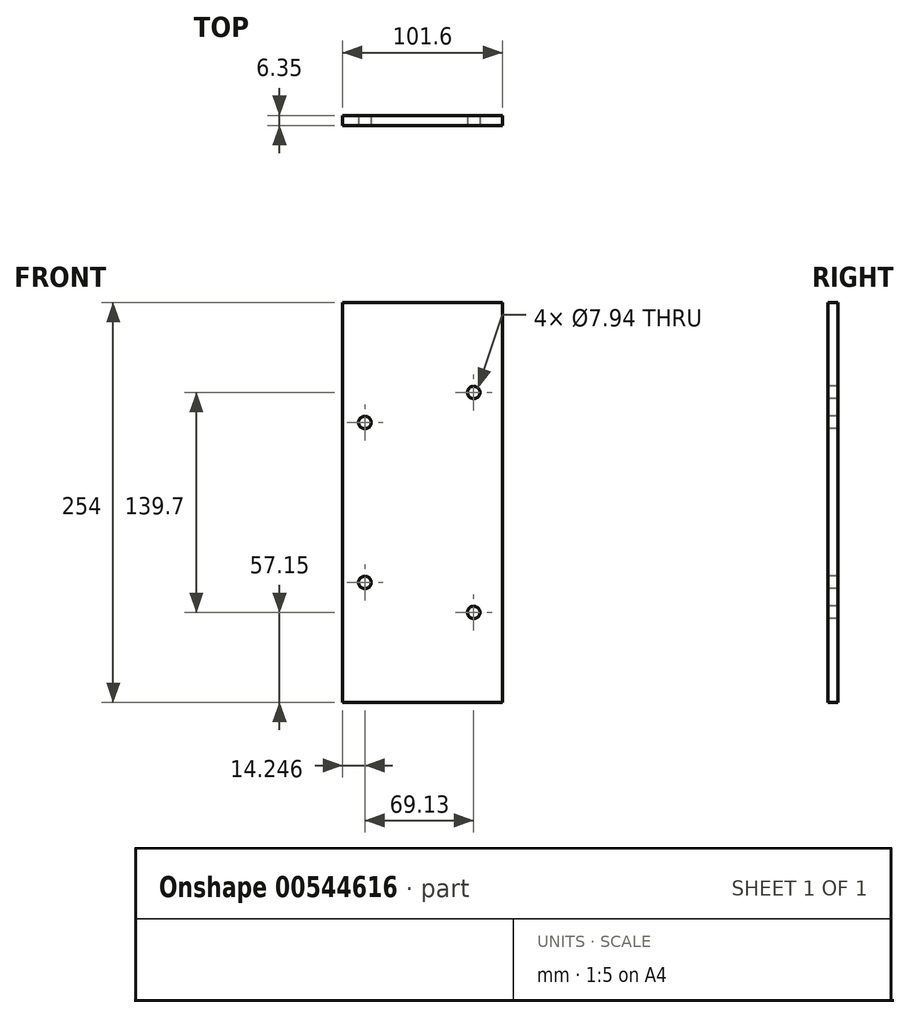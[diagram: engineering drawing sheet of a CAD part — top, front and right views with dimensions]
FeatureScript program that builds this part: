
annotation { "Feature Type Name" : "Feature", "Feature Type Description" : "" }
export const myFeature = defineFeature(function(context is Context, id is Id, definition is map)
    precondition{}
    {
        {
            var Q0;
            Q0=qCreatedBy(makeId("Front.planeOp"),FACE);
            var sketch = newSketch(context, id + "F0", { "sketchPlane" : qUnion([Q0])});
            skLineSegment(sketch, "E0.bottom", {"start": v(0, 0) * mm, "end": v(101.6, 0) * mm});
            skLineSegment(sketch, "E0.top", {"start": v(0, 254) * mm, "end": v(101.6, 254) * mm});
            skLineSegment(sketch, "E0.left", {"start": v(0, 0) * mm, "end": v(0, 254) * mm});
            skLineSegment(sketch, "E0.right", {"start": v(101.6, 0) * mm, "end": v(101.6, 254) * mm});
            skSolve(sketch);
        }
        {
            var Q0;
            Q0 = qSketchRegion(id + "F0", true);
            extrude(context, id + "F1", {"entities" : qUnion([Q0]), "depth" : 6.35 * mm, "offsetDistance" : 25.4 * mm});
        }
        {
            var Q0;
            Q0=makeQuery(id+"F1.opExtrude","CAP_FACE",FACE,{"disambiguationData":[OSD([sQuery(id+"F0.wireOp",EDGE,"E0.bottom"),sQuery(id+"F0.wireOp",EDGE,"E0.top"),sQuery(id+"F0.wireOp",EDGE,"E0.left"),sQuery(id+"F0.wireOp",EDGE,"E0.right")])],"isStart":false});
            var sketch = newSketch(context, id + "F2", { "sketchPlane" : qUnion([Q0])});
            skPoint(sketch, "E1", {"position": v(83.38, 57.15) * mm});
            skPoint(sketch, "E2", {"position": v(83.38, 196.85) * mm});
            skSolve(sketch);
        }
        {
            var Q0;
            Q0=sQuery(id+"F2.wireOp",VERTEX,"E1");
            var Q1;
            Q1=sQuery(id+"F2.wireOp",VERTEX,"E2");
            var Q2;
            Q2=makeQuery(id+"F1.opExtrude","SWEPT_BODY",BODY,{"disambiguationData":[OSD([sQuery(id+"F0.wireOp",EDGE,"E0.bottom"),sQuery(id+"F0.wireOp",EDGE,"E0.top"),sQuery(id+"F0.wireOp",EDGE,"E0.left"),sQuery(id+"F0.wireOp",EDGE,"E0.right")])]});
            hole(context, id + "F3", {"style" : HoleStyle.SIMPLE, "endStyle" : HoleEndStyle.THROUGH, "holeDiameter" : 7.94 * mm, "majorDiameter" : 6.35 * mm, "isTappedThrough" : true, "tappedDepth" : 12.7 * mm, "tapClearance" : 3, "locations" : qUnion([Q0, Q1]), "scope" : qUnion([Q2])});
        }
        {
            var Q0;
            Q0=makeQuery(id+"F1.opExtrude","CAP_FACE",FACE,{"disambiguationData":[OSD([sQuery(id+"F0.wireOp",EDGE,"E0.bottom"),sQuery(id+"F0.wireOp",EDGE,"E0.top"),sQuery(id+"F0.wireOp",EDGE,"E0.left"),sQuery(id+"F0.wireOp",EDGE,"E0.right")])],"isStart":false});
            var sketch = newSketch(context, id + "F4", { "sketchPlane" : qUnion([Q0])});
            skPoint(sketch, "E3", {"position": v(14.25, 76.2) * mm});
            skPoint(sketch, "E4", {"position": v(14.25, 177.8) * mm});
            skSolve(sketch);
        }
        {
            var Q0;
            Q0=sQuery(id+"F4.wireOp",VERTEX,"E3");
            var Q1;
            Q1=sQuery(id+"F4.wireOp",VERTEX,"E4");
            var Q2;
            Q2=makeQuery(id+"F1.opExtrude","SWEPT_BODY",BODY,{"disambiguationData":[OSD([sQuery(id+"F0.wireOp",EDGE,"E0.bottom"),sQuery(id+"F0.wireOp",EDGE,"E0.top"),sQuery(id+"F0.wireOp",EDGE,"E0.left"),sQuery(id+"F0.wireOp",EDGE,"E0.right")])]});
            hole(context, id + "F5", {"style" : HoleStyle.SIMPLE, "endStyle" : HoleEndStyle.THROUGH, "holeDiameter" : 7.94 * mm, "majorDiameter" : 6.35 * mm, "isTappedThrough" : true, "tappedDepth" : 12.7 * mm, "tapClearance" : 3, "locations" : qUnion([Q0, Q1]), "scope" : qUnion([Q2])});
        }
    });
